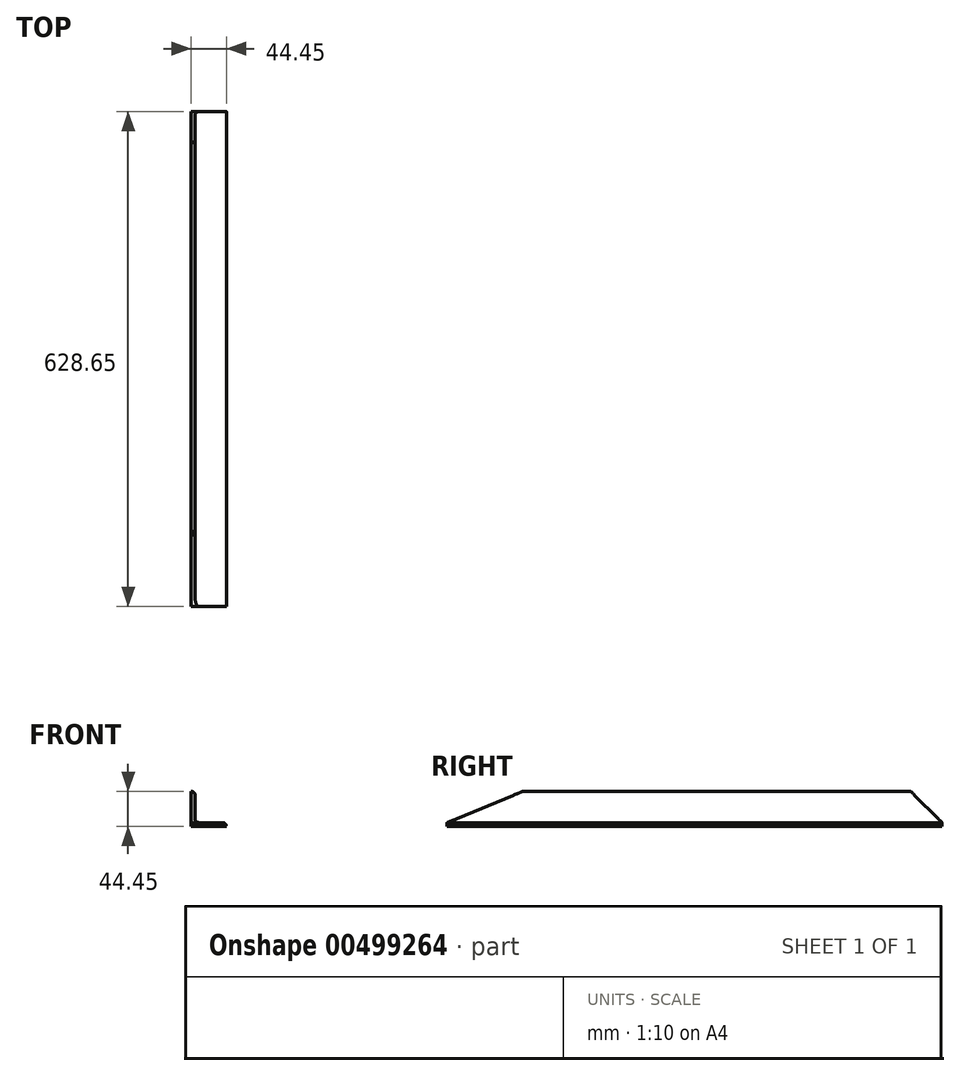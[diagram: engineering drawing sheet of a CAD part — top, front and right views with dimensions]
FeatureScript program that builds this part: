
annotation { "Feature Type Name" : "Feature", "Feature Type Description" : "" }
export const myFeature = defineFeature(function(context is Context, id is Id, definition is map)
    precondition{}
    {
        {
            var Q0;
            Q0=qCreatedBy(makeId("Front.planeOp"),FACE);
            var sketch = newSketch(context, id + "F0", { "sketchPlane" : qUnion([Q0])});
            skLineSegment(sketch, "E0", {"start": v(0, 0) * mm, "end": v(0, 44.45) * mm});
            skLineSegment(sketch, "E1", {"start": v(0, 0) * mm, "end": v(44.45, 0) * mm});
            skLineSegment(sketch, "E2", {"start": v(44.45, 0) * mm, "end": v(44.45, 4.76) * mm});
            skLineSegment(sketch, "E3", {"start": v(0, 44.45) * mm, "end": v(4.76, 44.45) * mm});
            skLineSegment(sketch, "E4", {"start": v(4.76, 44.45) * mm, "end": v(4.76, 4.76) * mm});
            skLineSegment(sketch, "E5", {"start": v(4.76, 4.76) * mm, "end": v(44.45, 4.76) * mm});
            skSolve(sketch);
        }
        {
            var Q0;
            Q0 = qSketchRegion(id + "F0", true);
            extrude(context, id + "F1", {"entities" : qUnion([Q0]), "depth" : 628.65 * mm});
        }
        {
            var Q0;
            Q0=makeQuery(id+"F1.opExtrude","SWEPT_EDGE",EDGE,{"disambiguationData":[OSD([sQuery(id+"F0.wireOp",EDGE,"E4"),sQuery(id+"F0.wireOp",EDGE,"E5")])]});
            var Q1;
            Q1=makeQuery(id+"F1.opExtrude","SWEPT_EDGE",EDGE,{"disambiguationData":[OSD([sQuery(id+"F0.wireOp",EDGE,"E3"),sQuery(id+"F0.wireOp",EDGE,"E4")])]});
            var Q2;
            Q2=makeQuery(id+"F1.opExtrude","SWEPT_EDGE",EDGE,{"disambiguationData":[OSD([sQuery(id+"F0.wireOp",EDGE,"E2"),sQuery(id+"F0.wireOp",EDGE,"E5")])]});
            fillet(context, id + "F2", {"entities" : qUnion([Q0, Q1, Q2]), "radius" : 4.76 * mm, "tangentPropagation" : true, "allowEdgeOverflow" : false});
        }
        {
            var Q0;
            Q0=makeQuery(id+"F1.opExtrude","SWEPT_FACE",FACE,{"disambiguationData":[OSD([sQuery(id+"F0.wireOp",EDGE,"E0")])]});
            var sketch = newSketch(context, id + "F3", { "sketchPlane" : qUnion([Q0])});
            skPoint(sketch, "E6.0", {"position": v(0, 4.76) * mm});
            skPoint(sketch, "E7.0", {"position": v(628.65, 4.76) * mm});
            skLineSegment(sketch, "E8", {"start": v(0, 4.76) * mm, "end": v(48.69, 4.76) * mm, "construction": true});
            skLineSegment(sketch, "E9", {"start": v(0, 4.76) * mm, "end": v(61.98, 66.74) * mm, "construction": true});
            skLineSegment(sketch, "E10", {"start": v(0, 4.76) * mm, "end": v(48.69, 4.76) * mm});
            skLineSegment(sketch, "E11", {"start": v(0, 4.76) * mm, "end": v(61.98, 66.74) * mm});
            skLineSegment(sketch, "E12", {"start": v(628.65, 4.76) * mm, "end": v(537.2, 4.76) * mm});
            skLineSegment(sketch, "E13", {"start": v(628.65, 4.76) * mm, "end": v(532.51, 44.58) * mm});
            skSolve(sketch);
        }
        {
            var Q0;
            Q0 = qSketchRegion(id + "F3", true);
            var Q1;
            {var subQ0=sQuery(id+"F3.wireOp",EDGE,"E11");var subQ1=sQuery(id+"F0.wireOp",EDGE,"E0");var subQ2=makeQuery(id+"F1.opExtrude","CAP_EDGE",EDGE,{"disambiguationData":[OSD([subQ1])],"isStart":true});var subQ3=makeQuery(id+"F3.imprint","INTERSECT",VERTEX,{"derivedFrom":[subQ2,subQ0]});Q1=makeQuery(id+"F3.imprint","IMPRINT",FACE,{"disambiguationData":[TD([[makeQuery(id+"F3.imprint","IMPRINT",EDGE,{"disambiguationData":[TD([[subQ3,-1.0]])],"derivedFrom":subQ0}),1.0]])]});}
            var Q2;
            {var subQ0=sQuery(id+"F3.wireOp",EDGE,"E13");var subQ1=sQuery(id+"F0.wireOp",EDGE,"E0");var subQ2=makeQuery(id+"F1.opExtrude","CAP_EDGE",EDGE,{"disambiguationData":[OSD([subQ1])],"isStart":false});var subQ3=makeQuery(id+"F3.imprint","INTERSECT",VERTEX,{"derivedFrom":[subQ2,subQ0]});Q2=makeQuery(id+"F3.imprint","IMPRINT",FACE,{"disambiguationData":[TD([[makeQuery(id+"F3.imprint","IMPRINT",EDGE,{"disambiguationData":[TD([[subQ3,-1.0]])],"derivedFrom":subQ0}),-1.0]])]});}
            extrude(context, id + "F4", {"entities" : qUnion([Q0, Q1, Q2]), "operationType" : NewBodyOperationType.REMOVE, "oppositeDirection" : true, "depth" : 25.4 * mm});
        }
    });
